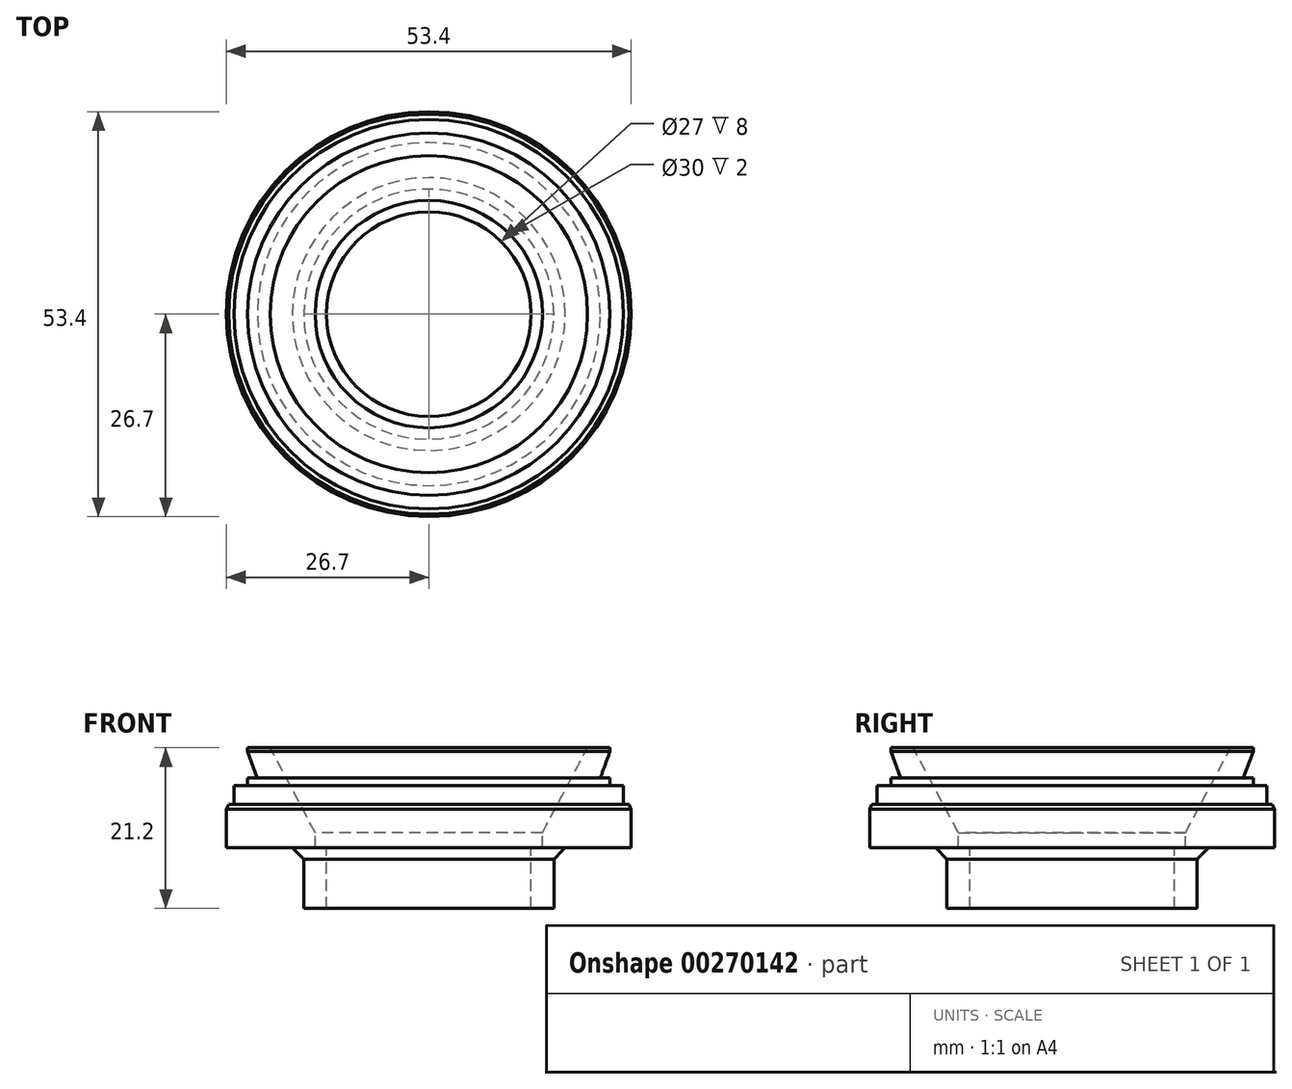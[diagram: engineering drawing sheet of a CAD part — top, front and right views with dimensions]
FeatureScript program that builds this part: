
annotation { "Feature Type Name" : "Feature", "Feature Type Description" : "" }
export const myFeature = defineFeature(function(context is Context, id is Id, definition is map)
    precondition{}
    {
        {
            var Q0;
            Q0=qCreatedBy(makeId("Front.planeOp"),FACE);
            var sketch = newSketch(context, id + "F0", { "sketchPlane" : qUnion([Q0])});
            skLineSegment(sketch, "E0", {"start": v(0, 0) * mm, "end": v(38.11, 0) * mm, "construction": true});
            skLineSegment(sketch, "E1", {"start": v(20.93, -22.8) * mm, "end": v(23.9, -22.8) * mm});
            skLineSegment(sketch, "E2", {"start": v(23.9, -22.8) * mm, "end": v(23.9, -23.3) * mm});
            skLineSegment(sketch, "E3", {"start": v(23.9, -23.3) * mm, "end": v(22.63, -26.8) * mm});
            skLineSegment(sketch, "E4", {"start": v(22.63, -26.8) * mm, "end": v(23.9, -26.8) * mm});
            skLineSegment(sketch, "E5", {"start": v(23.9, -26.8) * mm, "end": v(23.9, -27.8) * mm});
            skLineSegment(sketch, "E6", {"start": v(23.9, -27.8) * mm, "end": v(25.7, -27.8) * mm});
            skLineSegment(sketch, "E7", {"start": v(26.7, -30.9) * mm, "end": v(26.7, -36) * mm});
            skLineSegment(sketch, "E8", {"start": v(26.7, -36) * mm, "end": v(18, -36) * mm});
            skLineSegment(sketch, "E9", {"start": v(16.5, -37.5) * mm, "end": v(16.5, -44) * mm});
            skLineSegment(sketch, "E10", {"start": v(16.5, -44) * mm, "end": v(13.5, -44) * mm});
            skLineSegment(sketch, "E11", {"start": v(13.5, -44) * mm, "end": v(13.5, -36) * mm});
            skLineSegment(sketch, "E12", {"start": v(13.5, -36) * mm, "end": v(15, -36) * mm});
            skLineSegment(sketch, "E13", {"start": v(15, -36) * mm, "end": v(15, -34) * mm});
            skLineSegment(sketch, "E14", {"start": v(0, 0) * mm, "end": v(0, -18.86) * mm, "construction": true});
            skLineSegment(sketch, "E15", {"start": v(25.7, -27.8) * mm, "end": v(25.7, -30.3) * mm});
            skLineSegment(sketch, "E16", {"start": v(26.4, -30.3) * mm, "end": v(25.7, -30.3) * mm});
            skLineSegment(sketch, "E17", {"start": v(26.4, -30.3) * mm, "end": v(26.7, -30.9) * mm});
            skPoint(sketch, "E18.orphan", {"position": v(26.7, -30.3) * mm});
            skLineSegment(sketch, "E19", {"start": v(20.93, -22.8) * mm, "end": v(15, -34) * mm});
            skLineSegment(sketch, "E20", {"start": v(16.5, -37.5) * mm, "end": v(18, -36) * mm});
            skPoint(sketch, "E21.orphan", {"position": v(16.5, -36) * mm});
            skSolve(sketch);
        }
        {
            var Q0;
            Q0=makeQuery(id+"F0.imprint","IMPRINT",FACE,{"disambiguationData":[TD([[makeQuery(id+"F0.imprint","IMPRINT",EDGE,{"derivedFrom":sQuery(id+"F0.wireOp",EDGE,"E1")}),-1.0]])]});
            var Q1;
            Q1=sQuery(id+"F0.wireOp",EDGE,"E14");
            revolve(context, id + "F1", {"entities" : qUnion([Q0]), "axis" : qUnion([Q1]), "revolveType" : RevolveType.FULL});
        }
    });
